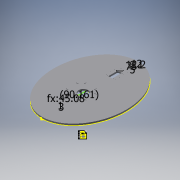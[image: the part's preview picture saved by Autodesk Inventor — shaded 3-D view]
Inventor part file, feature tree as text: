
AUTODESK INVENTOR PART (.ipt)
format: ipt  version: 2018 (Build 220112000, 112)  size: 532,480 bytes
history: native  units: in
note: dims shown in document units (in); Inventor stores cm internally (conversion verified against a paired STEP export)
features: reference x30, other x14, sketch x7, extrude x4
ambient origin geometry x8: Origin, YZ Plane, XZ Plane, XY Plane, X Axis, Y Axis, Z Axis, Center Point
bodies: Body1 (feature_tree)
feature tree (55):
  extrude  "Extrusion2"  Depth=0.3937in
  sketch  "Sketch2"  dims[d4=0.3937in d5=0.0in d6=0.1969in]
  sketch  "Sketch3"  dims[d7=0.1969in d24=0.5in]
  sketch  "Sketch8"  dims[d25=1.0in d31=3.5496in]
  extrude  "Extrusion13"  Depth=0.5in
  extrude  "Extrusion14"  Depth=1.0in
  extrude  "Extrusion15"  Depth=0.0394in
  sketch  "Sketch11"  dims[d48=0.0787in d49=0.1575in]
  sketch  "Sketch12"  dims[d58=0.0787in d59=0.1575in d60=0.0787in d61=0.1575in d62=0.0787in d63=0.1575in d64=0.0787in d65=0.1575in d66=0.0787in d67=0.1575in d68=0.0787in d69=0.1575in d70=0.0787in d71=0.1575in d73=0.1575in d74=0.0787in d75=0.1575in d76=0.0787in d77=0.1575in d78=0.0787in d79=0.1575in d80=0.0787in d81=0.1575in d82=0.0787in d83=0.1575in d84=0.0787in d85=0.1575in d86=0.0787in d87=0.1575in d88=0.3937in d89=0.0in d90=2.9528in d91=2.9528in d92=0.1437in d93=0.1437in d94=0.5in d95=0.3937in d96=0.0in d97=0.3937in d98=0.0in d99=2.9528in d100=0.1969in d103=0.4724in d104=0.2402in d105=0.4803in d108=9.36in d109=18.72in d110=7.0in]
  reference  "Reference1"
  reference  "Reference2"
  reference  "Reference3"
  reference  "Reference4"
  reference  "Reference7"
  reference  "Reference8"
  reference  "Reference9"
  reference  "Reference10"
  reference  "Reference11"
  sketch  "Sketch9"  dims[d32=1.7748in d36=0.0394in]
  reference  "Reference12"
  reference  "Reference13"
  reference  "Reference14"
  reference  "Reference15"
  reference  "Reference16"
  reference  "Reference17"
  reference  "Reference18"
  reference  "Reference19"
  reference  "Reference20"
  reference  "Reference21"
  reference  "Reference22"
  reference  "Reference23"
  reference  "Reference24"
  reference  "Reference25"
  reference  "Reference26"
  reference  "Reference27"
  sketch  "Sketch10"  dims[d37=0.1181in]
  reference  "Reference28"
  reference  "Reference29"
  reference  "Reference30"
  reference  "Reference31"
  reference  "Reference32"
  other  "<userpath>\OneDrive\Documents\Inventor\TSA\2018\Animatronics\Tortoise\AssemblyTURTLE.iam"
  other  "AssemblyTURTLE.iam"
  other  "wheelframe:1"
  other  "wheelframe2:1"
  other  "correct_wheel:1"
  other  "smallergear:1"
  other  "steer_servo_mount:1"
  other  "holder_gear_mount:1"
  other  "holder_gear_mount:2"
  other  "holder_gear_mount:3"
  other  "BackWheelMount:2"
  other  "BackWheelMount:1"
  other  "TailAssembly:1"
  other  "Tail_Servo_Mount:1"
